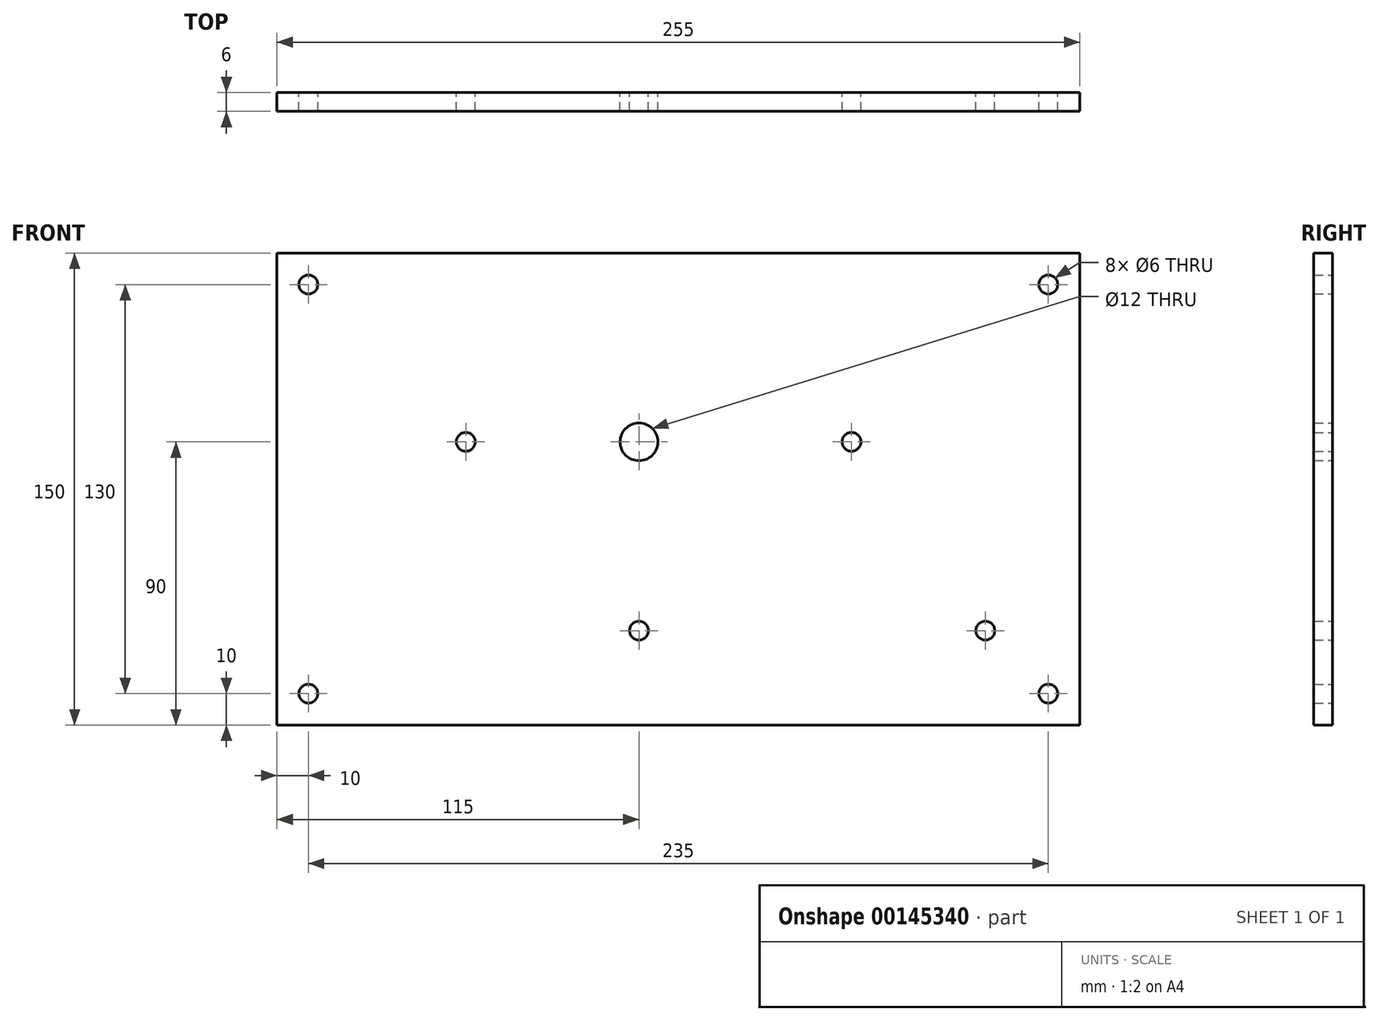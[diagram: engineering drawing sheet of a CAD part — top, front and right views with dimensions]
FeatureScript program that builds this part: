
annotation { "Feature Type Name" : "Feature", "Feature Type Description" : "" }
export const myFeature = defineFeature(function(context is Context, id is Id, definition is map)
    precondition{}
    {
        {
            var Q0;
            Q0=qCreatedBy(makeId("Front.planeOp"),FACE);
            var sketch = newSketch(context, id + "F0", { "sketchPlane" : qUnion([Q0])});
            skCircle(sketch, "E0", {"center": v(0, 0) * mm, "radius": 3 * mm});
            skCircle(sketch, "E1", {"center": v(55, 0) * mm, "radius": 6 * mm});
            skCircle(sketch, "E2", {"center": v(55, -60) * mm, "radius": 3 * mm});
            skCircle(sketch, "E3", {"center": v(165, -60) * mm, "radius": 3 * mm});
            skLineSegment(sketch, "E4", {"start": v(55, -60) * mm, "end": v(192.3, -60) * mm, "construction": true});
            skLineSegment(sketch, "E5.bottom", {"start": v(-60, 60) * mm, "end": v(195, 60) * mm});
            skLineSegment(sketch, "E5.top", {"start": v(-60, -90) * mm, "end": v(195, -90) * mm});
            skLineSegment(sketch, "E5.left", {"start": v(-60, 60) * mm, "end": v(-60, -90) * mm});
            skLineSegment(sketch, "E5.right", {"start": v(195, 60) * mm, "end": v(195, -90) * mm});
            skLineSegment(sketch, "E6", {"start": v(-60, 50) * mm, "end": v(195, 50) * mm, "construction": true});
            skLineSegment(sketch, "E7", {"start": v(-60, -80) * mm, "end": v(195, -80) * mm, "construction": true});
            skLineSegment(sketch, "E8", {"start": v(-50, 60) * mm, "end": v(-50, -90) * mm, "construction": true});
            skLineSegment(sketch, "E9", {"start": v(185, 60) * mm, "end": v(185, -90) * mm, "construction": true});
            skCircle(sketch, "E10", {"center": v(0, 0) * mm, "radius": 49.74 * mm, "construction": true});
            skCircle(sketch, "E11", {"center": v(-50, 50) * mm, "radius": 3 * mm});
            skCircle(sketch, "E12", {"center": v(-50, -80) * mm, "radius": 3 * mm});
            skCircle(sketch, "E13", {"center": v(185, 50) * mm, "radius": 3 * mm});
            skCircle(sketch, "E14", {"center": v(185, -80) * mm, "radius": 3 * mm});
            skLineSegment(sketch, "E15", {"start": v(0, 0) * mm, "end": v(155.37, 0) * mm, "construction": true});
            skCircle(sketch, "E16", {"center": v(122.5, 0) * mm, "radius": 3 * mm});
            skSolve(sketch);
        }
        {
            var Q0;
            Q0=makeQuery(id+"F0.imprint","IMPRINT",FACE,{"disambiguationData":[TD([[makeQuery(id+"F0.imprint","IMPRINT",EDGE,{"derivedFrom":sQuery(id+"F0.wireOp",EDGE,"E0")}),-1.0]])]});
            extrude(context, id + "F1", {"entities" : qUnion([Q0]), "depth" : 6 * mm});
        }
    });
